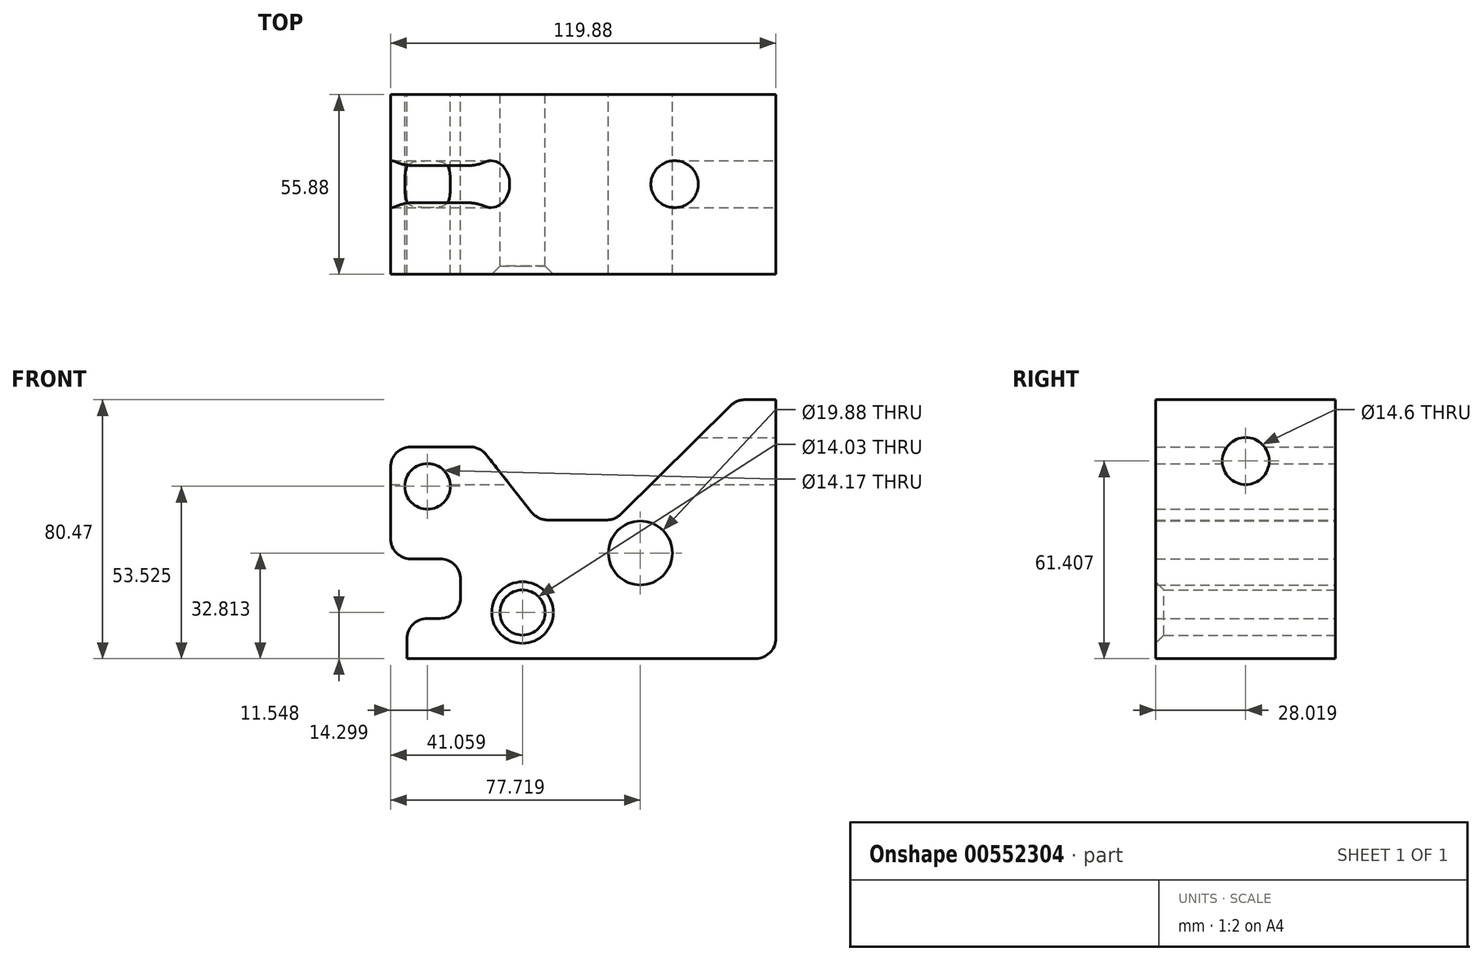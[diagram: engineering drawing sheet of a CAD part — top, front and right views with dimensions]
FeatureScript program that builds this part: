
annotation { "Feature Type Name" : "Feature", "Feature Type Description" : "" }
export const myFeature = defineFeature(function(context is Context, id is Id, definition is map)
    precondition{}
    {
        {
            var Q0;
            Q0=qCreatedBy(makeId("Front.planeOp"),FACE);
            var sketch = newSketch(context, id + "F0", { "sketchPlane" : qUnion([Q0])});
            skLineSegment(sketch, "E0", {"start": v(-49.19, 45.92) * mm, "end": v(-30.75, 45.92) * mm});
            skLineSegment(sketch, "E1", {"start": v(-25.77, 43.5) * mm, "end": v(-11.62, 25.6) * mm});
            skLineSegment(sketch, "E2", {"start": v(-6.64, 23.19) * mm, "end": v(11.69, 23.19) * mm});
            skLineSegment(sketch, "E3", {"start": v(16.15, 25.03) * mm, "end": v(50.2, 58.74) * mm});
            skLineSegment(sketch, "E4", {"start": v(54.67, 60.58) * mm, "end": v(64.34, 60.58) * mm});
            skLineSegment(sketch, "E5", {"start": v(64.34, 60.58) * mm, "end": v(64.34, -13.54) * mm});
            skLineSegment(sketch, "E6", {"start": v(57.99, -19.89) * mm, "end": v(-50.4, -19.89) * mm});
            skLineSegment(sketch, "E7", {"start": v(-50.4, -19.89) * mm, "end": v(-50.4, -13.77) * mm});
            skLineSegment(sketch, "E8", {"start": v(-44.06, -7.42) * mm, "end": v(-40.08, -7.42) * mm});
            skLineSegment(sketch, "E9", {"start": v(-33.73, -1.07) * mm, "end": v(-33.73, 4.74) * mm});
            skLineSegment(sketch, "E10", {"start": v(-40.08, 11.09) * mm, "end": v(-49.19, 11.09) * mm});
            skLineSegment(sketch, "E11", {"start": v(-55.54, 17.44) * mm, "end": v(-55.54, 39.57) * mm});
            skPoint(sketch, "E12.visualSharp", {"position": v(-55.54, 45.92) * mm});
            skArc(sketch, "E12.filletArc", {"start": v(-49.19, 45.92) * mm, "mid": v(-53.68, 44.06) * mm, "end": v(-55.54, 39.57) * mm});
            skPoint(sketch, "E13.visualSharp", {"position": v(-27.68, 45.92) * mm});
            skArc(sketch, "E13.filletArc", {"start": v(-25.77, 43.5) * mm, "mid": v(-27.99, 45.28) * mm, "end": v(-30.75, 45.92) * mm});
            skPoint(sketch, "E14.visualSharp", {"position": v(-9.71, 23.19) * mm});
            skArc(sketch, "E14.filletArc", {"start": v(-11.62, 25.6) * mm, "mid": v(-9.4, 23.82) * mm, "end": v(-6.64, 23.19) * mm});
            skPoint(sketch, "E15.visualSharp", {"position": v(14.3, 23.19) * mm});
            skArc(sketch, "E15.filletArc", {"start": v(11.69, 23.19) * mm, "mid": v(14.1, 23.66) * mm, "end": v(16.15, 25.03) * mm});
            skPoint(sketch, "E16.visualSharp", {"position": v(52.06, 60.58) * mm});
            skArc(sketch, "E16.filletArc", {"start": v(54.67, 60.58) * mm, "mid": v(52.25, 60.1) * mm, "end": v(50.2, 58.74) * mm});
            skPoint(sketch, "E17.visualSharp", {"position": v(64.34, -19.89) * mm});
            skArc(sketch, "E17.filletArc", {"start": v(57.99, -19.89) * mm, "mid": v(62.48, -18.03) * mm, "end": v(64.34, -13.54) * mm});
            skPoint(sketch, "E18.visualSharp", {"position": v(-55.54, 11.09) * mm});
            skArc(sketch, "E18.filletArc", {"start": v(-55.54, 17.44) * mm, "mid": v(-53.68, 12.95) * mm, "end": v(-49.19, 11.09) * mm});
            skPoint(sketch, "E19.visualSharp", {"position": v(-33.73, 11.09) * mm});
            skArc(sketch, "E19.filletArc", {"start": v(-33.73, 4.74) * mm, "mid": v(-35.59, 9.23) * mm, "end": v(-40.08, 11.09) * mm});
            skPoint(sketch, "E20.visualSharp", {"position": v(-33.73, -7.42) * mm});
            skArc(sketch, "E20.filletArc", {"start": v(-40.08, -7.42) * mm, "mid": v(-35.59, -5.56) * mm, "end": v(-33.73, -1.07) * mm});
            skPoint(sketch, "E21.visualSharp", {"position": v(-50.4, -7.42) * mm});
            skArc(sketch, "E21.filletArc", {"start": v(-44.06, -7.42) * mm, "mid": v(-48.55, -9.28) * mm, "end": v(-50.4, -13.77) * mm});
            skCircle(sketch, "E22", {"center": v(22.18, 12.92) * mm, "radius": 9.94 * mm});
            skCircle(sketch, "E23", {"center": v(-14.48, -5.6) * mm, "radius": 7.02 * mm});
            skCircle(sketch, "E24", {"center": v(-44, 33.64) * mm, "radius": 7.08 * mm});
            skCircle(sketch, "E25", {"center": v(48.02, -7.8) * mm, "radius": 7.67 * mm});
            skSolve(sketch);
        }
        {
            var Q0;
            Q0=makeQuery(id+"F0.imprint","IMPRINT",FACE,{"disambiguationData":[TD([[makeQuery(id+"F0.imprint","IMPRINT",EDGE,{"derivedFrom":sQuery(id+"F0.wireOp",EDGE,"E0")}),-1.0]])]});
            var Q1;
            Q1=makeQuery(id+"F0.imprint","IMPRINT",FACE,{"disambiguationData":[TD([[makeQuery(id+"F0.imprint","IMPRINT",EDGE,{"derivedFrom":sQuery(id+"F0.wireOp",EDGE,"E25")}),1.0]])]});
            extrude(context, id + "F1", {"entities" : qUnion([Q0, Q1]), "depth" : 55.88 * mm, "offsetDistance" : 25.4 * mm});
        }
        {
            var Q0;
            Q0=makeQuery(id+"F1.opExtrude","SWEPT_FACE",FACE,{"disambiguationData":[OSD([sQuery(id+"F0.wireOp",EDGE,"E5")])]});
            var sketch = newSketch(context, id + "F2", { "sketchPlane" : qUnion([Q0])});
            skCircle(sketch, "E26", {"center": v(-27.86, 41.52) * mm, "radius": 7.3 * mm});
            skSolve(sketch);
        }
        {
            var Q0;
            Q0=makeQuery(id+"F2.imprint","IMPRINT",FACE,{"disambiguationData":[TD([[makeQuery(id+"F2.imprint","IMPRINT",EDGE,{"derivedFrom":sQuery(id+"F2.wireOp",EDGE,"E26")}),1.0]])]});
            var Q1;
            Q1=makeQuery(id+"F1.opExtrude","SWEPT_FACE",FACE,{"disambiguationData":[OSD([sQuery(id+"F0.wireOp",EDGE,"E11")])]});
            extrude(context, id + "F3", {"entities" : qUnion([Q0, Q1]), "operationType" : NewBodyOperationType.REMOVE, "endBound" : BoundingType.THROUGH_ALL, "oppositeDirection" : true, "depth" : 25.4 * mm, "offsetDistance" : 25.4 * mm});
        }
        {
            var Q0;
            Q0=makeQuery(id+"F1.opExtrude","CAP_EDGE",EDGE,{"disambiguationData":[OSD([sQuery(id+"F0.wireOp",EDGE,"E23")])],"isStart":false});
            chamfer(context, id + "F4", {"entities" : qUnion([Q0]), "width" : 2.54 * mm, "tangentPropagation" : true});
        }
    });
